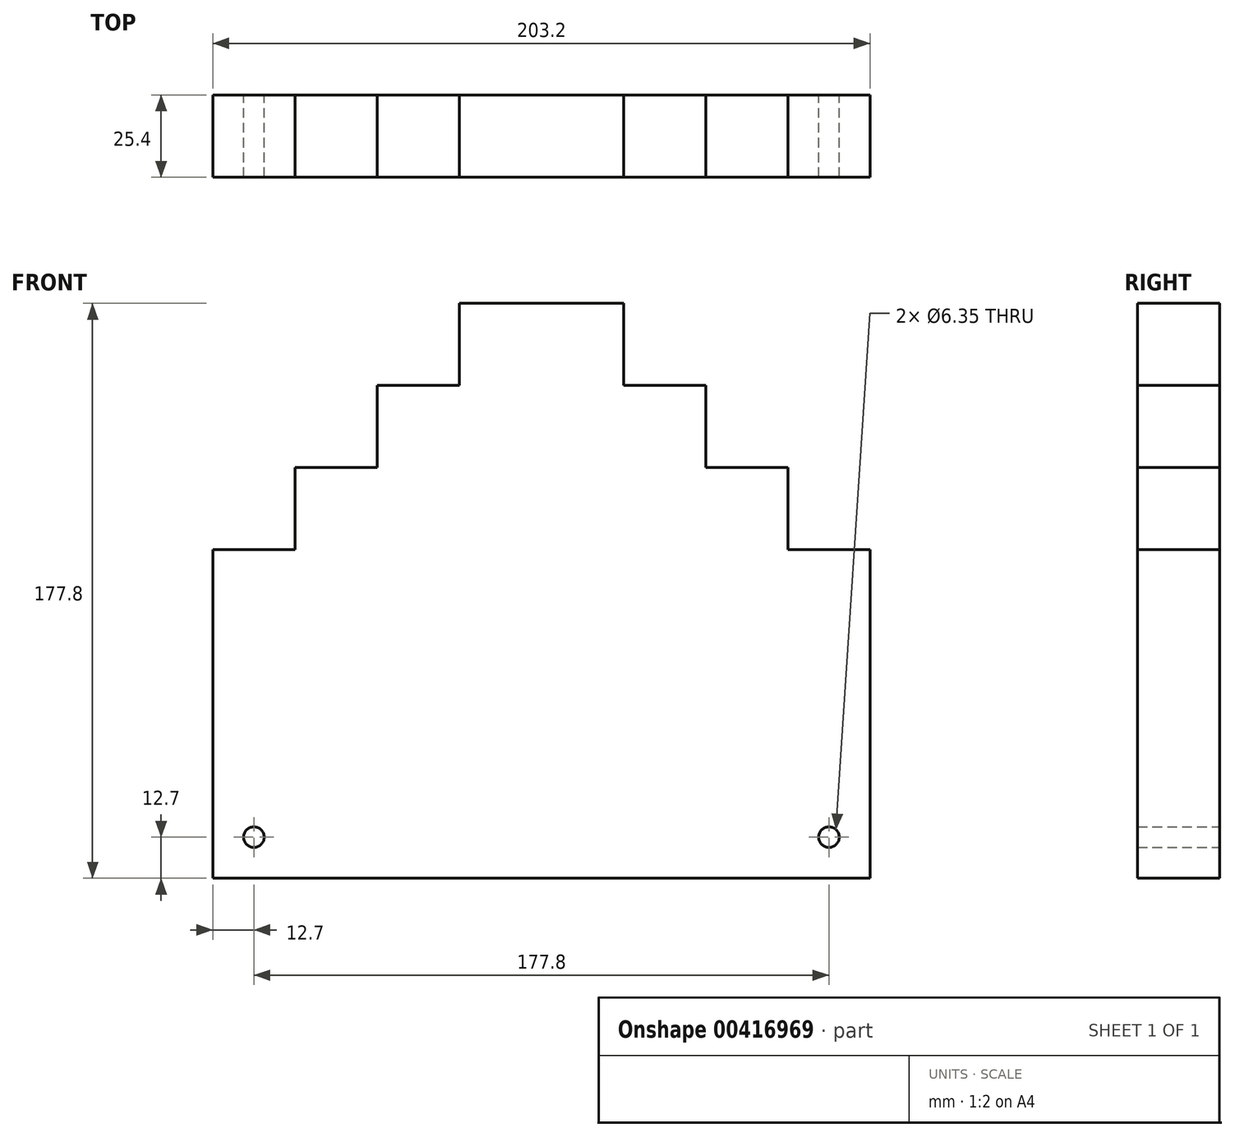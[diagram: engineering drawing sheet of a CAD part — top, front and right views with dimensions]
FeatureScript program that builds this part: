
annotation { "Feature Type Name" : "Feature", "Feature Type Description" : "" }
export const myFeature = defineFeature(function(context is Context, id is Id, definition is map)
    precondition{}
    {
        {
            var Q0;
            Q0=qCreatedBy(makeId("Front.planeOp"),FACE);
            var sketch = newSketch(context, id + "F0", { "sketchPlane" : qUnion([Q0])});
            skLineSegment(sketch, "E0", {"start": v(-349.7, 0) * mm, "end": v(338.04, 0) * mm, "construction": true});
            skLineSegment(sketch, "E1.bottom", {"start": v(0, 0) * mm, "end": v(-25.4, 0) * mm});
            skLineSegment(sketch, "E1.top", {"start": v(0, 177.8) * mm, "end": v(-25.4, 177.8) * mm});
            skLineSegment(sketch, "E1.left", {"start": v(0, 0) * mm, "end": v(0, 177.8) * mm});
            skLineSegment(sketch, "E1.right", {"start": v(-25.4, 0) * mm, "end": v(-25.4, 177.8) * mm});
            skLineSegment(sketch, "E2.bottom", {"start": v(0, 177.8) * mm, "end": v(25.4, 177.8) * mm});
            skLineSegment(sketch, "E2.top", {"start": v(0, 0) * mm, "end": v(25.4, 0) * mm});
            skLineSegment(sketch, "E2.left", {"start": v(0, 177.8) * mm, "end": v(0, 0) * mm});
            skLineSegment(sketch, "E2.right", {"start": v(25.4, 177.8) * mm, "end": v(25.4, 0) * mm});
            skLineSegment(sketch, "E3.bottom", {"start": v(25.4, 152.4) * mm, "end": v(50.8, 152.4) * mm});
            skLineSegment(sketch, "E3.top", {"start": v(25.4, 0) * mm, "end": v(50.8, 0) * mm});
            skLineSegment(sketch, "E3.left", {"start": v(25.4, 152.4) * mm, "end": v(25.4, 0) * mm});
            skLineSegment(sketch, "E3.right", {"start": v(50.8, 152.4) * mm, "end": v(50.8, 0) * mm});
            skLineSegment(sketch, "E4.bottom", {"start": v(-25.4, 152.4) * mm, "end": v(-50.8, 152.4) * mm});
            skLineSegment(sketch, "E4.top", {"start": v(-25.4, 0) * mm, "end": v(-50.8, 0) * mm});
            skLineSegment(sketch, "E4.left", {"start": v(-25.4, 152.4) * mm, "end": v(-25.4, 0) * mm});
            skLineSegment(sketch, "E5", {"start": v(-50.8, 152.4) * mm, "end": v(-50.8, 0) * mm});
            skLineSegment(sketch, "E6.bottom", {"start": v(50.8, 127) * mm, "end": v(76.2, 127) * mm});
            skLineSegment(sketch, "E6.top", {"start": v(50.8, 0) * mm, "end": v(76.2, 0) * mm});
            skLineSegment(sketch, "E6.left", {"start": v(50.8, 127) * mm, "end": v(50.8, 0) * mm});
            skLineSegment(sketch, "E6.right", {"start": v(76.2, 127) * mm, "end": v(76.2, 0) * mm});
            skLineSegment(sketch, "E7.bottom", {"start": v(-50.8, 127) * mm, "end": v(-76.2, 127) * mm});
            skLineSegment(sketch, "E7.top", {"start": v(-50.8, 0) * mm, "end": v(-76.2, 0) * mm});
            skLineSegment(sketch, "E7.left", {"start": v(-50.8, 127) * mm, "end": v(-50.8, 0) * mm});
            skLineSegment(sketch, "E7.right", {"start": v(-76.2, 127) * mm, "end": v(-76.2, 0) * mm});
            skLineSegment(sketch, "E8.bottom", {"start": v(-76.2, 101.6) * mm, "end": v(-101.6, 101.6) * mm});
            skLineSegment(sketch, "E8.top", {"start": v(-76.2, 0) * mm, "end": v(-101.6, 0) * mm});
            skLineSegment(sketch, "E8.left", {"start": v(-76.2, 101.6) * mm, "end": v(-76.2, 0) * mm});
            skLineSegment(sketch, "E8.right", {"start": v(-101.6, 101.6) * mm, "end": v(-101.6, 0) * mm});
            skLineSegment(sketch, "E9.bottom", {"start": v(76.2, 101.6) * mm, "end": v(101.6, 101.6) * mm});
            skLineSegment(sketch, "E9.top", {"start": v(76.2, 0) * mm, "end": v(101.6, 0) * mm});
            skLineSegment(sketch, "E9.left", {"start": v(76.2, 101.6) * mm, "end": v(76.2, 0) * mm});
            skLineSegment(sketch, "E9.right", {"start": v(101.6, 101.6) * mm, "end": v(101.6, 0) * mm});
            skCircle(sketch, "E10", {"center": v(-88.9, 12.7) * mm, "radius": 3.18 * mm});
            skPoint(sketch, "E10.centerSnap0", {"position": v(-88.9, 0) * mm});
            skCircle(sketch, "E11", {"center": v(88.9, 12.7) * mm, "radius": 3.18 * mm});
            skPoint(sketch, "E11.centerSnap0", {"position": v(88.9, 0) * mm});
            skSolve(sketch);
        }
        {
            var Q0;
            Q0=makeQuery(id+"F0.imprint","IMPRINT",FACE,{"disambiguationData":[TD([[makeQuery(id+"F0.imprint","IMPRINT",EDGE,{"derivedFrom":sQuery(id+"F0.wireOp",EDGE,"E8.bottom")}),1.0]])]});
            var Q1;
            Q1=makeQuery(id+"F0.imprint","IMPRINT",FACE,{"disambiguationData":[TD([[makeQuery(id+"F0.imprint","IMPRINT",EDGE,{"derivedFrom":sQuery(id+"F0.wireOp",EDGE,"E7.bottom")}),1.0]])]});
            var Q2;
            Q2=makeQuery(id+"F0.imprint","IMPRINT",FACE,{"disambiguationData":[TD([[makeQuery(id+"F0.imprint","IMPRINT",EDGE,{"derivedFrom":sQuery(id+"F0.wireOp",EDGE,"E4.bottom")}),1.0]])]});
            var Q3;
            Q3=makeQuery(id+"F0.imprint","IMPRINT",FACE,{"disambiguationData":[TD([[makeQuery(id+"F0.imprint","IMPRINT",EDGE,{"derivedFrom":sQuery(id+"F0.wireOp",EDGE,"E1.bottom")}),-1.0]])]});
            var Q4;
            Q4=makeQuery(id+"F0.imprint","IMPRINT",FACE,{"disambiguationData":[TD([[makeQuery(id+"F0.imprint","IMPRINT",EDGE,{"derivedFrom":sQuery(id+"F0.wireOp",EDGE,"E2.bottom")}),-1.0]])]});
            var Q5;
            Q5=makeQuery(id+"F0.imprint","IMPRINT",FACE,{"disambiguationData":[TD([[makeQuery(id+"F0.imprint","IMPRINT",EDGE,{"derivedFrom":sQuery(id+"F0.wireOp",EDGE,"E3.bottom")}),-1.0]])]});
            var Q6;
            Q6=makeQuery(id+"F0.imprint","IMPRINT",FACE,{"disambiguationData":[TD([[makeQuery(id+"F0.imprint","IMPRINT",EDGE,{"derivedFrom":sQuery(id+"F0.wireOp",EDGE,"E6.bottom")}),-1.0]])]});
            var Q7;
            Q7=makeQuery(id+"F0.imprint","IMPRINT",FACE,{"disambiguationData":[TD([[makeQuery(id+"F0.imprint","IMPRINT",EDGE,{"derivedFrom":sQuery(id+"F0.wireOp",EDGE,"E9.bottom")}),-1.0]])]});
            extrude(context, id + "F1", {"entities" : qUnion([Q0, Q1, Q2, Q3, Q4, Q5, Q6, Q7]), "depth" : 25.4 * mm});
        }
    });
